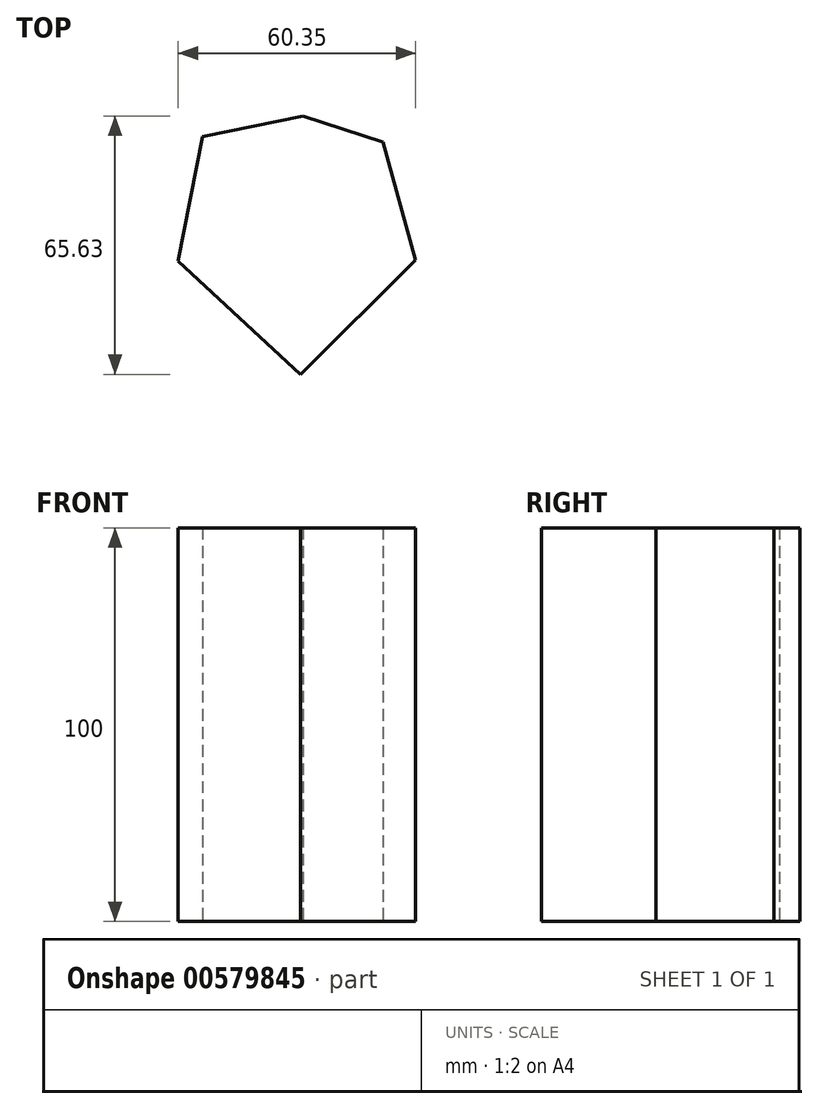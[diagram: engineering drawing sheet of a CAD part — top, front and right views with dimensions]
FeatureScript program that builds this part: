
annotation { "Feature Type Name" : "Feature", "Feature Type Description" : "" }
export const myFeature = defineFeature(function(context is Context, id is Id, definition is map)
    precondition{}
    {
        {
            var Q0;
            Q0=qCreatedBy(makeId("Top.planeOp"),FACE);
            var sketch = newSketch(context, id + "F0", { "sketchPlane" : qUnion([Q0])});
            skLineSegment(sketch, "E0", {"start": v(29.26, -7.62) * mm, "end": v(0, -36.63) * mm});
            skLineSegment(sketch, "E1", {"start": v(0, -36.63) * mm, "end": v(-31.1, -7.89) * mm});
            skLineSegment(sketch, "E2", {"start": v(-31.1, -7.89) * mm, "end": v(-24.84, 23.82) * mm});
            skLineSegment(sketch, "E3", {"start": v(20.9, 22.4) * mm, "end": v(29.26, -7.62) * mm});
            skLineSegment(sketch, "E4", {"start": v(-24.84, 23.82) * mm, "end": v(0.6, 29) * mm});
            skLineSegment(sketch, "E5", {"start": v(0.6, 29) * mm, "end": v(20.9, 22.4) * mm});
            skLineSegment(sketch, "E6", {"start": v(-12.12, 26.4) * mm, "end": v(14.63, -22.12) * mm, "construction": true});
            skLineSegment(sketch, "E7", {"start": v(10.75, 25.7) * mm, "end": v(-15.55, -22.26) * mm, "construction": true});
            skLineSegment(sketch, "E8", {"start": v(-27.97, 7.96) * mm, "end": v(25.07, 7.4) * mm, "construction": true});
            skSolve(sketch);
        }
        {
            var Q0;
            Q0 = qSketchRegion(id + "F0", true);
            extrude(context, id + "F1", {"entities" : qUnion([Q0]), "depth" : 100 * mm, "offsetDistance" : 25 * mm});
        }
    });
